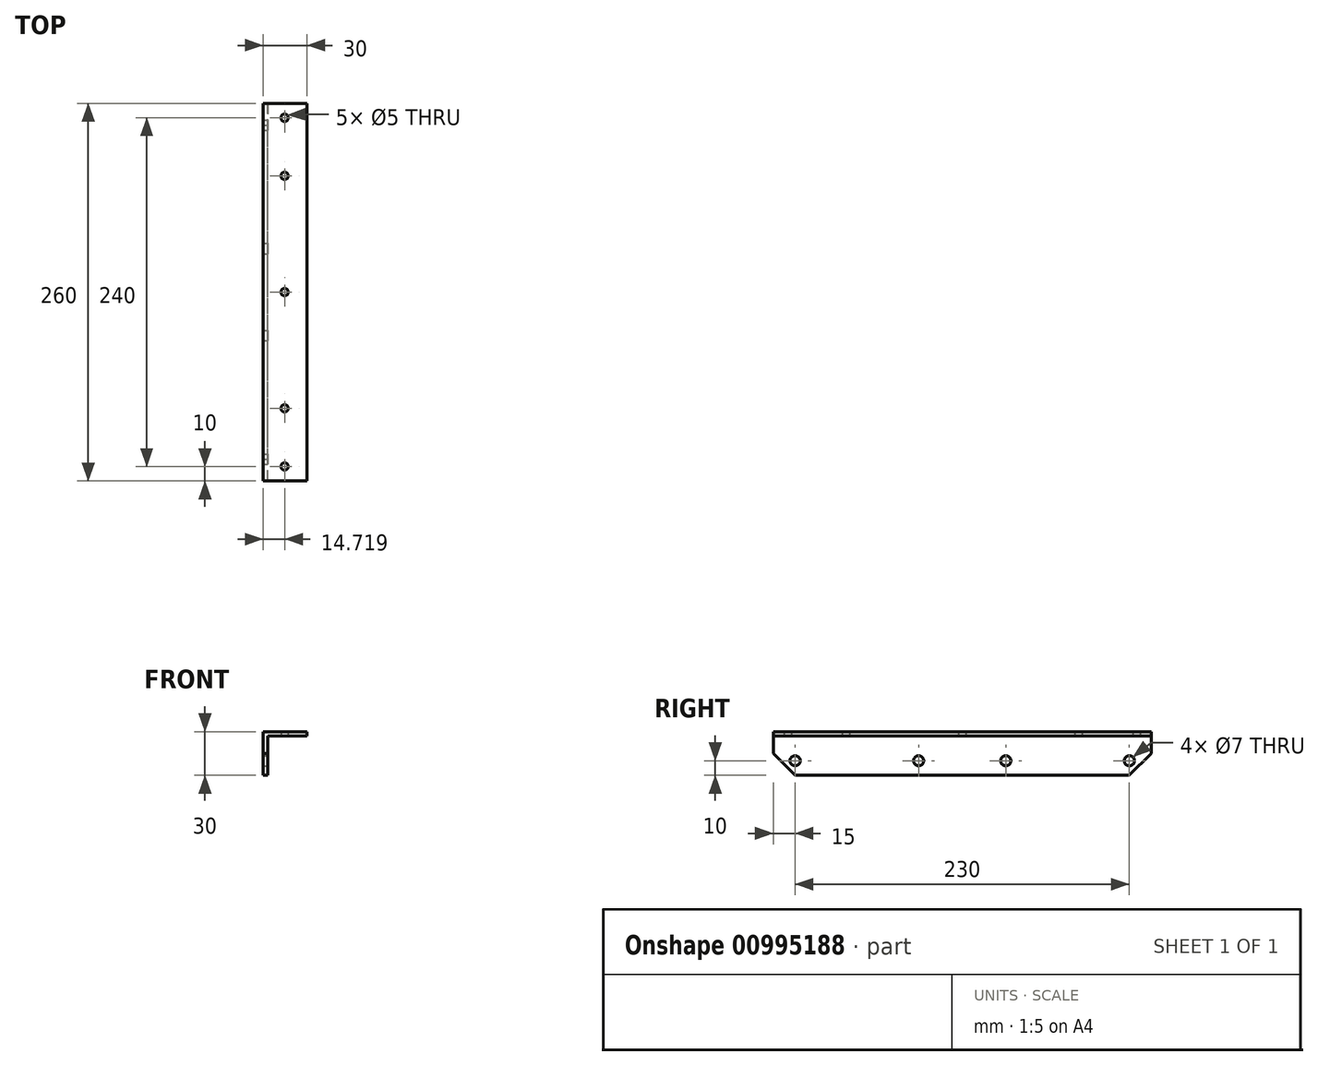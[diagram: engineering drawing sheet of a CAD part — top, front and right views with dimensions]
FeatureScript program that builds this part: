
annotation { "Feature Type Name" : "Feature", "Feature Type Description" : "" }
export const myFeature = defineFeature(function(context is Context, id is Id, definition is map)
    precondition{}
    {
        {
            var Q0;
            Q0=qCreatedBy(makeId("Front.planeOp"),FACE);
            var sketch = newSketch(context, id + "F0", { "sketchPlane" : qUnion([Q0])});
            skLineSegment(sketch, "E0", {"start": v(0, 0) * mm, "end": v(0, 30) * mm});
            skLineSegment(sketch, "E1", {"start": v(0, 30) * mm, "end": v(30, 30) * mm});
            skLineSegment(sketch, "E2", {"start": v(30, 30) * mm, "end": v(30, 27) * mm});
            skLineSegment(sketch, "E3", {"start": v(30, 27) * mm, "end": v(3, 27) * mm});
            skLineSegment(sketch, "E4", {"start": v(3, 27) * mm, "end": v(3, 0) * mm});
            skLineSegment(sketch, "E5", {"start": v(3, 0) * mm, "end": v(0, 0) * mm});
            skSolve(sketch);
        }
        {
            var Q0;
            Q0=makeQuery(id+"F0.imprint","IMPRINT",FACE,{"disambiguationData":[TD([[makeQuery(id+"F0.imprint","IMPRINT",EDGE,{"derivedFrom":sQuery(id+"F0.wireOp",EDGE,"E0")}),-1.0]])]});
            extrude(context, id + "F1", {"entities" : qUnion([Q0]), "depth" : 260 * mm, "offsetDistance" : 25 * mm, "symmetric" : true});
        }
        {
            var Q0;
            Q0=makeQuery(id+"F1.opExtrude","SWEPT_FACE",FACE,{"disambiguationData":[OSD([sQuery(id+"F0.wireOp",EDGE,"E0")])]});
            var sketch = newSketch(context, id + "F2", { "sketchPlane" : qUnion([Q0])});
            skLineSegment(sketch, "E6", {"start": v(0, 30) * mm, "end": v(0, 10) * mm});
            skLineSegment(sketch, "E7", {"start": v(115, 10) * mm, "end": v(130, 10) * mm});
            skLineSegment(sketch, "E8", {"start": v(-115, 10) * mm, "end": v(-130, 10) * mm});
            skLineSegment(sketch, "E9", {"start": v(-115, 10) * mm, "end": v(30, 10) * mm});
            skLineSegment(sketch, "E10", {"start": v(115, 10) * mm, "end": v(-30, 10) * mm});
            skSolve(sketch);
        }
        {
            var Q0;
            Q0=sQuery(id+"F2.wireOp",VERTEX,"h4xNsvRR-XN5t-T3dQ-VFSg-j4WRrjtfRfhr.end");
            var Q1;
            Q1=sQuery(id+"F2.wireOp",VERTEX,"Ygrv8C5C-21mS-Lryx-x8Gy-2dsrVxnptCvR.end");
            var Q2;
            Q2=sQuery(id+"F2.wireOp",VERTEX,"E9.start");
            var Q3;
            Q3=sQuery(id+"F2.wireOp",VERTEX,"E10.end");
            var Q4;
            Q4=sQuery(id+"F2.wireOp",VERTEX,"E9.end");
            var Q5;
            Q5=sQuery(id+"F2.wireOp",VERTEX,"E7.start");
            var Q6;
            Q6=makeQuery(id+"F1.opExtrude","SWEPT_BODY",BODY,{"disambiguationData":[OSD([sQuery(id+"F0.wireOp",EDGE,"E0"),sQuery(id+"F0.wireOp",EDGE,"E1"),sQuery(id+"F0.wireOp",EDGE,"E2"),sQuery(id+"F0.wireOp",EDGE,"E3"),sQuery(id+"F0.wireOp",EDGE,"E4"),sQuery(id+"F0.wireOp",EDGE,"E5")])]});
            hole(context, id + "F3", {"style" : HoleStyle.SIMPLE, "endStyle" : HoleEndStyle.THROUGH, "holeDiameter" : 7 * mm, "majorDiameter" : 5 * mm, "isTappedThrough" : true, "tappedDepth" : 12 * mm, "tapClearance" : 3, "locations" : qUnion([Q0, Q1, Q2, Q3, Q4, Q5]), "scope" : qUnion([Q6]), "startStyle" : HoleStartStyle.PART});
        }
        {
            var Q0;
            Q0=makeQuery(id+"F1.opExtrude","SWEPT_FACE",FACE,{"disambiguationData":[OSD([sQuery(id+"F0.wireOp",EDGE,"E1")])]});
            var sketch = newSketch(context, id + "F4", { "sketchPlane" : qUnion([Q0])});
            skLineSegment(sketch, "E11", {"start": v(0, 0) * mm, "end": v(14.72, 0) * mm});
            skLineSegment(sketch, "E12", {"start": v(14.72, 0) * mm, "end": v(14.72, 40) * mm});
            skLineSegment(sketch, "E13", {"start": v(14.72, 0) * mm, "end": v(14.72, -40) * mm});
            skLineSegment(sketch, "E14", {"start": v(14.72, -40) * mm, "end": v(14.72, -80) * mm});
            skLineSegment(sketch, "E15", {"start": v(14.72, -80) * mm, "end": v(14.72, -120) * mm});
            skLineSegment(sketch, "E16", {"start": v(14.72, 40) * mm, "end": v(14.72, 80) * mm});
            skLineSegment(sketch, "E17", {"start": v(14.72, 80) * mm, "end": v(14.72, 120) * mm});
            skSolve(sketch);
        }
        {
            var Q0;
            Q0=sQuery(id+"F4.wireOp",VERTEX,"E15.end");
            var Q1;
            Q1=sQuery(id+"F4.wireOp",VERTEX,"E14.end");
            var Q2;
            Q2=sQuery(id+"F4.wireOp",VERTEX,"E11.end");
            var Q3;
            Q3=sQuery(id+"F4.wireOp",VERTEX,"E16.end");
            var Q4;
            Q4=sQuery(id+"F4.wireOp",VERTEX,"E17.end");
            var Q5;
            Q5=makeQuery(id+"F1.opExtrude","SWEPT_BODY",BODY,{"disambiguationData":[OSD([sQuery(id+"F0.wireOp",EDGE,"E0"),sQuery(id+"F0.wireOp",EDGE,"E1"),sQuery(id+"F0.wireOp",EDGE,"E2"),sQuery(id+"F0.wireOp",EDGE,"E3"),sQuery(id+"F0.wireOp",EDGE,"E4"),sQuery(id+"F0.wireOp",EDGE,"E5")])]});
            hole(context, id + "F5", {"style" : HoleStyle.SIMPLE, "endStyle" : HoleEndStyle.THROUGH, "holeDiameter" : 5 * mm, "majorDiameter" : 5 * mm, "isTappedThrough" : true, "tappedDepth" : 12 * mm, "tapClearance" : 3, "locations" : qUnion([Q0, Q1, Q2, Q3, Q4]), "scope" : qUnion([Q5]), "startStyle" : HoleStartStyle.PART});
        }
        {
            var Q0;
            Q0=makeQuery(id+"F1.opExtrude","SWEPT_FACE",FACE,{"disambiguationData":[OSD([sQuery(id+"F0.wireOp",EDGE,"E4")])]});
            var sketch = newSketch(context, id + "F6", { "sketchPlane" : qUnion([Q0])});
            skLineSegment(sketch, "E18", {"start": v(-130, 0) * mm, "end": v(-130, 15) * mm});
            skLineSegment(sketch, "E19", {"start": v(-130, 15) * mm, "end": v(-115, 0) * mm});
            skLineSegment(sketch, "E20", {"start": v(-115, 0) * mm, "end": v(-130, 0) * mm});
            skLineSegment(sketch, "E21", {"start": v(130, 0) * mm, "end": v(130, 15) * mm});
            skLineSegment(sketch, "E22", {"start": v(130, 15) * mm, "end": v(115, 0) * mm});
            skLineSegment(sketch, "E23", {"start": v(115, 0) * mm, "end": v(130, 0) * mm});
            skSolve(sketch);
        }
        {
            var Q0;
            Q0=makeQuery(id+"F6.imprint","IMPRINT",FACE,{"disambiguationData":[TD([[makeQuery(id+"F6.imprint","IMPRINT",EDGE,{"derivedFrom":sQuery(id+"F6.wireOp",EDGE,"E18")}),1.0]])]});
            var Q1;
            Q1=makeQuery(id+"F6.imprint","IMPRINT",FACE,{"disambiguationData":[TD([[makeQuery(id+"F6.imprint","IMPRINT",EDGE,{"derivedFrom":sQuery(id+"F6.wireOp",EDGE,"E21")}),-1.0]])]});
            extrude(context, id + "F7", {"entities" : qUnion([Q0, Q1]), "operationType" : NewBodyOperationType.REMOVE, "oppositeDirection" : true, "depth" : 25 * mm, "offsetDistance" : 25 * mm});
        }
    });
